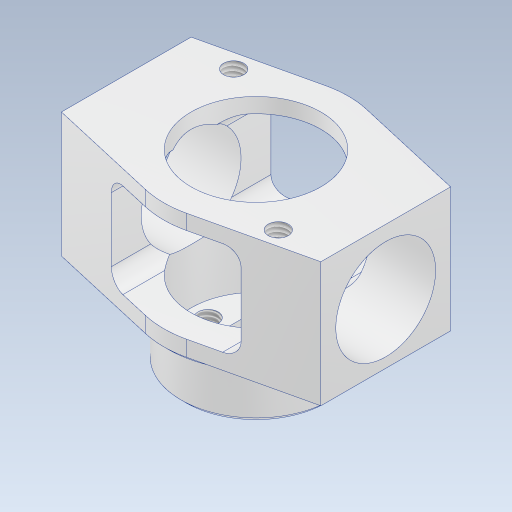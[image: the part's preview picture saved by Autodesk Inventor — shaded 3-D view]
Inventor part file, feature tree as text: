
AUTODESK INVENTOR PART (.ipt)
format: ipt  version: 2024 (Build 280153000, 153)  size: 326,144 bytes
history: native  units: mm
features: other x6, sketch x2, hole x2, fillet x1, extrude x1, chamfer x1
ambient origin geometry x8: Origin, YZ Plane, XZ Plane, XY Plane, X Axis, Y Axis, Z Axis, Center Point
bodies: Body1 (feature_tree)
feature tree (13):
  other  "_bridseye_sketch.ipt"
  fillet  "フィレット1"  Radius=10.0mm
  sketch  "スケッチ3"
  extrude  "押し出し1"  Depth=1.5mm
  hole  "穴1"  [1 undecoded]
  hole  "穴2"  [1 undecoded]
  chamfer  "面取り3"  [1 undecoded]
  other  "TaggingFeature1"
  other  "ソリッド9::_bridseye_sketch.ipt"
  other  "top_shoulderUnit-largeGearShaft_baseWasher"
  other  "front_shoulderUnit"
  other  "top_shoulderUnit-largeGearShaft_smallGearShaft"
  sketch  "スケッチ6"
note: 3 required parameter values undecoded (feature->parameter linkage not recoverable at this tier; creation-order binding heuristic only, values carry confidence <= 0.55)
